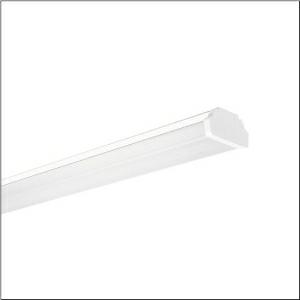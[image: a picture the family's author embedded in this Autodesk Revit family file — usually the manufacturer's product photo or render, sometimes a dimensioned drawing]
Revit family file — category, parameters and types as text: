
# Revit family: dus_31_gen_2_53bd812cv475c2_3345
name_source: partatom
category: Lighting Fixtures
units: mm (PartAtom-declared; Revit-internal decimal feet)

## family parameters
Cut with Voids When Loaded = No
Host = Face
Light Source = No
Part Type = Normal
Room Calculation Point = No
Round Connector Dimension = Use Diameter
Shared = No

## types (1)
- --- (1 x LED, 7600 lm, 40.5 W, 4000K)
    Apparent Load = 41 VA
    CIE Flux Codes = 47 80 95 93 100
    Color Rendering = 80
    Color Temperature = 4000K
    Default Elevation = 1800 mm
    Description = DUS 31 Gen.2, luminaire insert, of sheet steel, coil coated, white, length: 1.535mm, width: 81mm, height: 90mm, 5x system unit, system units: 307mm, LED rated luminous flux: 7.600lm, light colour: 840, SDCM (Standard Deviation of Colour Matching)MacAdam ≤ 3 SDCM (initial), control gear: ON/OFF Multilumen, CLOi, with plug, 3-pole, with phase selection, mains connection: 220..240V, AC, 50/60Hz, start of lifetime: 41W, end of service life: 48W, through-wiring accessed according to module size, primary optical cover: cover, of PMMA, light emission: direct distribution, primary light characteristic: symmetric, protection rating (complete): IP20, protection rating (LED compartment): IP50, insulation class (complete): insulation class I (protective earthing), certification: CE, ENEC, VDE, UKCA, impact resistance: IK03, permissible ambient temperature for indoor applications: -35..+50°C, corresponds to IFS (International Featured Standards) requirements for safety and quality in the food industry, reducing of maximum allowable ambient temperature of 5°C with ceiling mounting, packaging unit: 1 piece
    Height = 95 mm
    Lamp = 1 x LED
    Lamp Light Flux = 7600 lm
    Lamp Power = 40.5 W
    Lamp count = 1
    Length = 1535 mm
    Luminous efficacy = 188 lm/W
    Manufacturer = Siteco
    ModVariant = No
    Model = 53BD812CV475C2
    Mounting Place = Ceiling
    Mounting Type = Pendant
    Number of Poles = 1
    OnlyDefault = Yes
    Power Factor = 1
    Product Name = DUS 31 Gen.2
    Product group = luminaire insert | ceiling pendant
    ProductGroupID = 901
    Protection Class = Protection class I
    Protection Degree = IP 20
    RLX_Detail_Level = 1
    RLX_Emergency_Light_Flux = 0 lm
    RLX_Emergency_Type = 0
    RLX_Emergency_Type_DB = No
    RlxData = <blob elided: 29825 chars, md5=6e06b34a>
    Socket = socket
    Standby Power = 0 W
    System Light Flux = 7600 lm
    System Power = 41 W
    Type Comments = factory setting: luminous flux: 100 % | (A | C | E) | 94 mA
    Type Image = l_1319596.jpg
    URL = http://relux.com
    VarID = @adj_040819
    Voltage = 0 V
    Weight = 0.00 kg
    Width = 81 mm

## geometry (parser evidence)
native form markers: Blend x4, Sweep x10
no freeform markers — native parametric forms only
